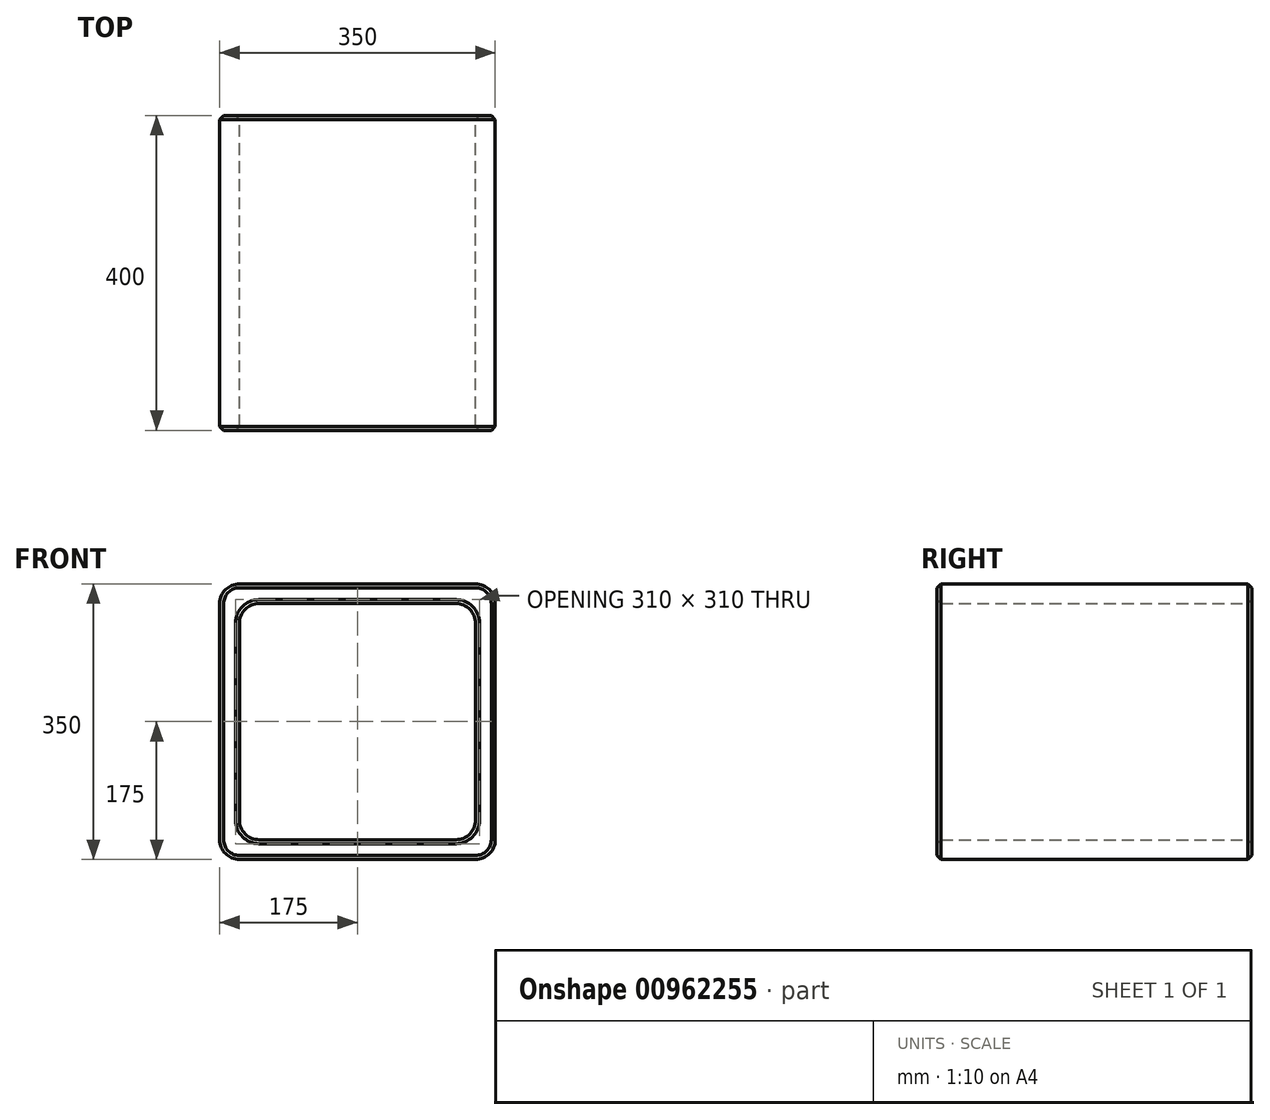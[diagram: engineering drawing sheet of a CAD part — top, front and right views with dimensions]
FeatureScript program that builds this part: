
annotation { "Feature Type Name" : "Feature", "Feature Type Description" : "" }
export const myFeature = defineFeature(function(context is Context, id is Id, definition is map)
    precondition{}
    {
        {
            var Q0;
            Q0=qCreatedBy(makeId("Front.planeOp"),FACE);
            var sketch = newSketch(context, id + "F0", { "sketchPlane" : qUnion([Q0])});
            skLineSegment(sketch, "E0.bottom", {"start": v(25, 0) * mm, "end": v(325, 0) * mm});
            skLineSegment(sketch, "E0.top", {"start": v(25, 350) * mm, "end": v(325, 350) * mm});
            skLineSegment(sketch, "E0.left", {"start": v(0, 25) * mm, "end": v(0, 325) * mm});
            skLineSegment(sketch, "E0.right", {"start": v(350, 25) * mm, "end": v(350, 325) * mm});
            skLineSegment(sketch, "E1.bottom", {"start": v(50, 325) * mm, "end": v(300, 325) * mm});
            skLineSegment(sketch, "E1.top", {"start": v(50, 25) * mm, "end": v(300, 25) * mm});
            skLineSegment(sketch, "E1.left", {"start": v(25, 300) * mm, "end": v(25, 50) * mm});
            skLineSegment(sketch, "E1.right", {"start": v(325, 300) * mm, "end": v(325, 50) * mm});
            skPoint(sketch, "E2.visualSharp", {"position": v(25, 325) * mm});
            skArc(sketch, "E2.filletArc", {"start": v(50, 325) * mm, "mid": v(32.32, 317.68) * mm, "end": v(25, 300) * mm});
            skPoint(sketch, "E3.visualSharp", {"position": v(0, 350) * mm});
            skArc(sketch, "E3.filletArc", {"start": v(25, 350) * mm, "mid": v(7.32, 342.68) * mm, "end": v(0, 325) * mm});
            skPoint(sketch, "E4.visualSharp", {"position": v(350, 350) * mm});
            skArc(sketch, "E4.filletArc", {"start": v(350, 325) * mm, "mid": v(342.68, 342.68) * mm, "end": v(325, 350) * mm});
            skArc(sketch, "E5.filletArc", {"start": v(325, 300) * mm, "mid": v(317.68, 317.68) * mm, "end": v(300, 325) * mm});
            skPoint(sketch, "E6.visualSharp", {"position": v(325, 25) * mm});
            skArc(sketch, "E6.filletArc", {"start": v(300, 25) * mm, "mid": v(317.68, 32.32) * mm, "end": v(325, 50) * mm});
            skPoint(sketch, "E7.visualSharp", {"position": v(350, 0) * mm});
            skArc(sketch, "E7.filletArc", {"start": v(325, 0) * mm, "mid": v(342.68, 7.32) * mm, "end": v(350, 25) * mm});
            skPoint(sketch, "E8.visualSharp", {"position": v(25, 25) * mm});
            skArc(sketch, "E8.filletArc", {"start": v(25, 50) * mm, "mid": v(32.32, 32.32) * mm, "end": v(50, 25) * mm});
            skPoint(sketch, "E9.visualSharp", {"position": v(0, 0) * mm});
            skArc(sketch, "E9.filletArc", {"start": v(0, 25) * mm, "mid": v(7.32, 7.32) * mm, "end": v(25, 0) * mm});
            skSolve(sketch);
        }
        {
            var Q0;
            Q0 = qSketchRegion(id + "F0", true);
            extrude(context, id + "F1", {"entities" : qUnion([Q0]), "depth" : 400 * mm, "offsetDistance" : 25 * mm});
        }
        {
            var Q0;
            Q0=makeQuery(id+"F1.opExtrude","CAP_EDGE",EDGE,{"disambiguationData":[OSD([sQuery(id+"F0.wireOp",EDGE,"E0.left")])],"isStart":false});
            var Q1;
            Q1=makeQuery(id+"F1.opExtrude","CAP_EDGE",EDGE,{"disambiguationData":[OSD([sQuery(id+"F0.wireOp",EDGE,"E1.left")])],"isStart":false});
            var Q2;
            Q2=makeQuery(id+"F1.opExtrude","CAP_EDGE",EDGE,{"disambiguationData":[OSD([sQuery(id+"F0.wireOp",EDGE,"E0.top")])],"isStart":true});
            var Q3;
            Q3=makeQuery(id+"F1.opExtrude","CAP_EDGE",EDGE,{"disambiguationData":[OSD([sQuery(id+"F0.wireOp",EDGE,"E1.bottom")])],"isStart":true});
            chamfer(context, id + "F2", {"entities" : qUnion([Q0, Q1, Q2, Q3]), "width" : 5 * mm, "tangentPropagation" : true});
        }
    });
